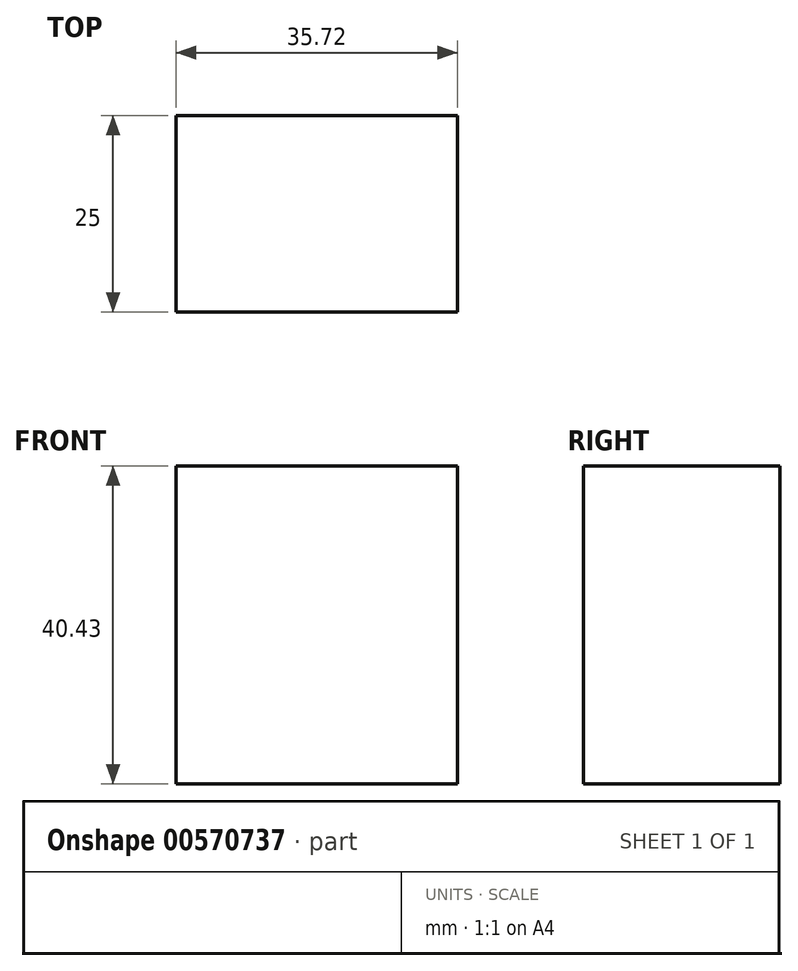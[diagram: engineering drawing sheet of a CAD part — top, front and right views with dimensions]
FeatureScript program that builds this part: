
annotation { "Feature Type Name" : "Feature", "Feature Type Description" : "" }
export const myFeature = defineFeature(function(context is Context, id is Id, definition is map)
    precondition{}
    {
        {
            var Q0;
            Q0=qCreatedBy(makeId("Front.planeOp"),FACE);
            var sketch = newSketch(context, id + "F0", { "sketchPlane" : qUnion([Q0])});
            skLineSegment(sketch, "E0.bottom", {"start": v(-69.43, 30.03) * mm, "end": v(-33.71, 30.03) * mm});
            skLineSegment(sketch, "E0.top", {"start": v(-69.43, -10.4) * mm, "end": v(-33.71, -10.4) * mm});
            skLineSegment(sketch, "E0.left", {"start": v(-69.43, 30.03) * mm, "end": v(-69.43, -10.4) * mm});
            skLineSegment(sketch, "E0.right", {"start": v(-33.71, 30.03) * mm, "end": v(-33.71, -10.4) * mm});
            skSolve(sketch);
        }
        {
            var Q0;
            Q0 = qSketchRegion(id + "F0", true);
            extrude(context, id + "F1", {"entities" : qUnion([Q0]), "depth" : 25 * mm, "offsetDistance" : 25 * mm});
        }
    });
